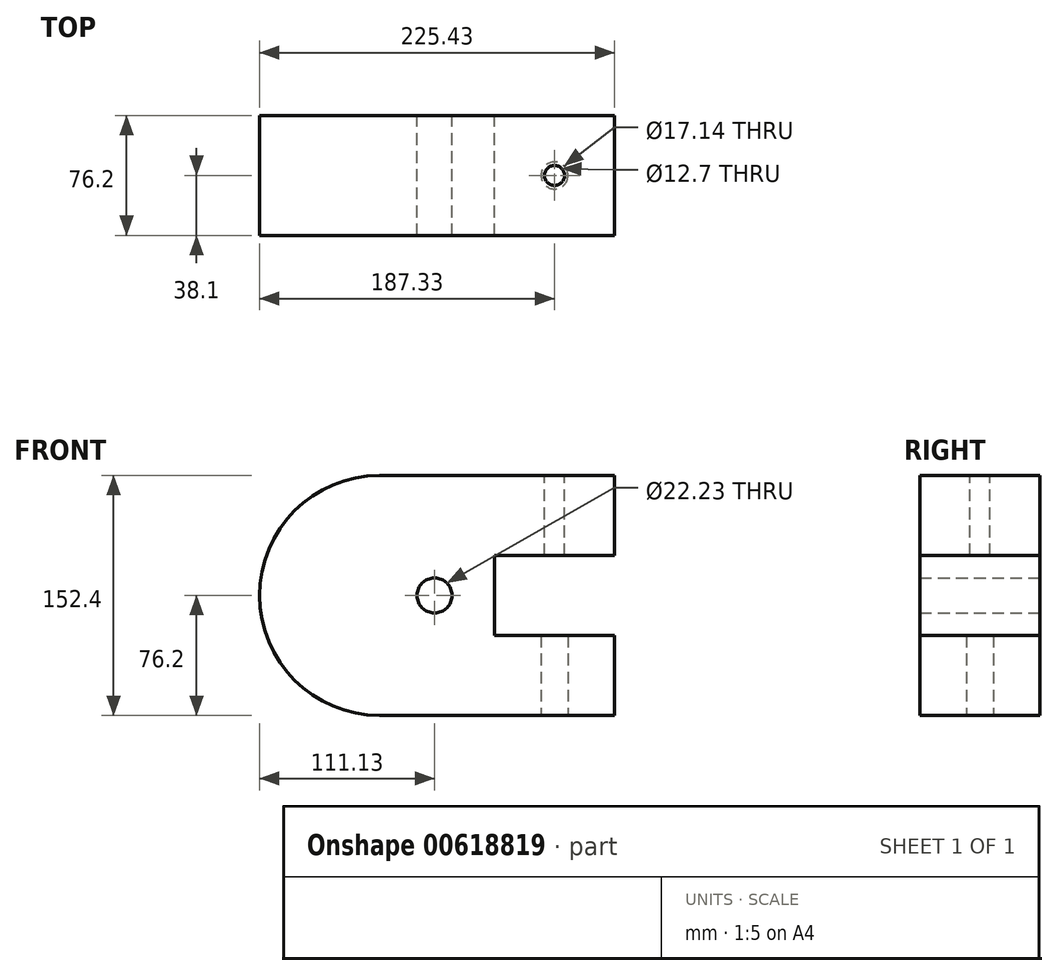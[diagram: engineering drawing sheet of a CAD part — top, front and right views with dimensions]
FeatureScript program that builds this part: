
annotation { "Feature Type Name" : "Feature", "Feature Type Description" : "" }
export const myFeature = defineFeature(function(context is Context, id is Id, definition is map)
    precondition{}
    {
        {
            var Q0;
            Q0=qCreatedBy(makeId("Front.planeOp"),FACE);
            var sketch = newSketch(context, id + "F0", { "sketchPlane" : qUnion([Q0])});
            skLineSegment(sketch, "E0", {"start": v(0, 0) * mm, "end": v(-149.22, 0) * mm});
            skLineSegment(sketch, "E1", {"start": v(-149.23, 0) * mm, "end": v(-149.23, 152.4) * mm});
            skLineSegment(sketch, "E2", {"start": v(-149.23, 152.4) * mm, "end": v(0, 152.4) * mm});
            skArc(sketch, "E3", {"start": v(-149.23, 152.4) * mm, "mid": v(-225.43, 76.2) * mm, "end": v(-149.22, 0) * mm});
            skLineSegment(sketch, "E4", {"start": v(0, 152.4) * mm, "end": v(0, 101.6) * mm});
            skLineSegment(sketch, "E5", {"start": v(0, 101.6) * mm, "end": v(-76.2, 101.6) * mm});
            skLineSegment(sketch, "E6", {"start": v(-76.2, 101.6) * mm, "end": v(-76.2, 50.8) * mm});
            skLineSegment(sketch, "E7", {"start": v(-76.2, 50.8) * mm, "end": v(0, 50.8) * mm});
            skLineSegment(sketch, "E8", {"start": v(0, 50.8) * mm, "end": v(0, 0) * mm});
            skSolve(sketch);
        }
        {
            var Q0;
            Q0 = qSketchRegion(id + "F0", true);
            extrude(context, id + "F1", {"entities" : qUnion([Q0]), "depth" : 76.2 * mm, "offsetDistance" : 25.4 * mm});
        }
        {
            var Q0;
            Q0=qCreatedBy(makeId("Top.planeOp"),FACE);
            var sketch = newSketch(context, id + "F2", { "sketchPlane" : qUnion([Q0])});
            skCircle(sketch, "E9", {"center": v(-38.1, -38.1) * mm, "radius": 8.57 * mm});
            skSolve(sketch);
        }
        {
            var Q0;
            Q0=sQuery(id+"F2.wireOp",VERTEX,"E9.center");
            var Q1;
            Q1=makeQuery(id+"F1.opExtrude","SWEPT_BODY",BODY,{"disambiguationData":[OSD([sQuery(id+"F0.wireOp",EDGE,"E0"),sQuery(id+"F0.wireOp",EDGE,"E2"),sQuery(id+"F0.wireOp",EDGE,"E3"),sQuery(id+"F0.wireOp",EDGE,"E4"),sQuery(id+"F0.wireOp",EDGE,"E5"),sQuery(id+"F0.wireOp",EDGE,"E6"),sQuery(id+"F0.wireOp",EDGE,"E7"),sQuery(id+"F0.wireOp",EDGE,"E8")])]});
            hole(context, id + "F3", {"style" : HoleStyle.SIMPLE, "endStyle" : HoleEndStyle.BLIND, "oppositeDirection" : true, "holeDiameter" : 17.14 * mm, "majorDiameter" : 6.35 * mm, "holeDepth" : 50.8 * mm, "isTappedThrough" : true, "tappedDepth" : 12.7 * mm, "tapClearance" : 3, "locations" : qUnion([Q0]), "scope" : qUnion([Q1])});
        }
        {
            var Q0;
            Q0=makeQuery(id+"F1.opExtrude","SWEPT_FACE",FACE,{"disambiguationData":[OSD([sQuery(id+"F0.wireOp",EDGE,"E2")])]});
            var sketch = newSketch(context, id + "F4", { "sketchPlane" : qUnion([Q0])});
            skCircle(sketch, "E10", {"center": v(-38.1, -38.1) * mm, "radius": 6.35 * mm});
            skSolve(sketch);
        }
        {
            var Q0;
            Q0=sQuery(id+"F4.wireOp",VERTEX,"E10.center");
            var Q1;
            Q1=makeQuery(id+"F1.opExtrude","SWEPT_BODY",BODY,{"disambiguationData":[OSD([sQuery(id+"F0.wireOp",EDGE,"E0"),sQuery(id+"F0.wireOp",EDGE,"E2"),sQuery(id+"F0.wireOp",EDGE,"E3"),sQuery(id+"F0.wireOp",EDGE,"E4"),sQuery(id+"F0.wireOp",EDGE,"E5"),sQuery(id+"F0.wireOp",EDGE,"E6"),sQuery(id+"F0.wireOp",EDGE,"E7"),sQuery(id+"F0.wireOp",EDGE,"E8")])]});
            hole(context, id + "F5", {"style" : HoleStyle.SIMPLE, "endStyle" : HoleEndStyle.BLIND, "holeDiameter" : 12.7 * mm, "majorDiameter" : 6.35 * mm, "holeDepth" : 50.8 * mm, "isTappedThrough" : true, "tappedDepth" : 12.7 * mm, "tapClearance" : 3, "locations" : qUnion([Q0]), "scope" : qUnion([Q1])});
        }
        {
            var Q0;
            Q0=makeQuery(id+"F1.opExtrude","CAP_FACE",FACE,{"disambiguationData":[OSD([sQuery(id+"F0.wireOp",EDGE,"E0"),sQuery(id+"F0.wireOp",EDGE,"E2"),sQuery(id+"F0.wireOp",EDGE,"E3"),sQuery(id+"F0.wireOp",EDGE,"E4"),sQuery(id+"F0.wireOp",EDGE,"E5"),sQuery(id+"F0.wireOp",EDGE,"E6"),sQuery(id+"F0.wireOp",EDGE,"E7"),sQuery(id+"F0.wireOp",EDGE,"E8")])],"isStart":true});
            var sketch = newSketch(context, id + "F6", { "sketchPlane" : qUnion([Q0])});
            skCircle(sketch, "E11", {"center": v(114.3, 76.2) * mm, "radius": 11.11 * mm});
            skSolve(sketch);
        }
        {
            var Q0;
            Q0=sQuery(id+"F6.wireOp",VERTEX,"E11.center");
            var Q1;
            Q1=makeQuery(id+"F1.opExtrude","SWEPT_BODY",BODY,{"disambiguationData":[OSD([sQuery(id+"F0.wireOp",EDGE,"E0"),sQuery(id+"F0.wireOp",EDGE,"E2"),sQuery(id+"F0.wireOp",EDGE,"E3"),sQuery(id+"F0.wireOp",EDGE,"E4"),sQuery(id+"F0.wireOp",EDGE,"E5"),sQuery(id+"F0.wireOp",EDGE,"E6"),sQuery(id+"F0.wireOp",EDGE,"E7"),sQuery(id+"F0.wireOp",EDGE,"E8")])]});
            hole(context, id + "F7", {"style" : HoleStyle.SIMPLE, "endStyle" : HoleEndStyle.THROUGH, "holeDiameter" : 22.22 * mm, "majorDiameter" : 6.35 * mm, "isTappedThrough" : true, "tappedDepth" : 12.7 * mm, "tapClearance" : 3, "locations" : qUnion([Q0]), "scope" : qUnion([Q1])});
        }
    });
